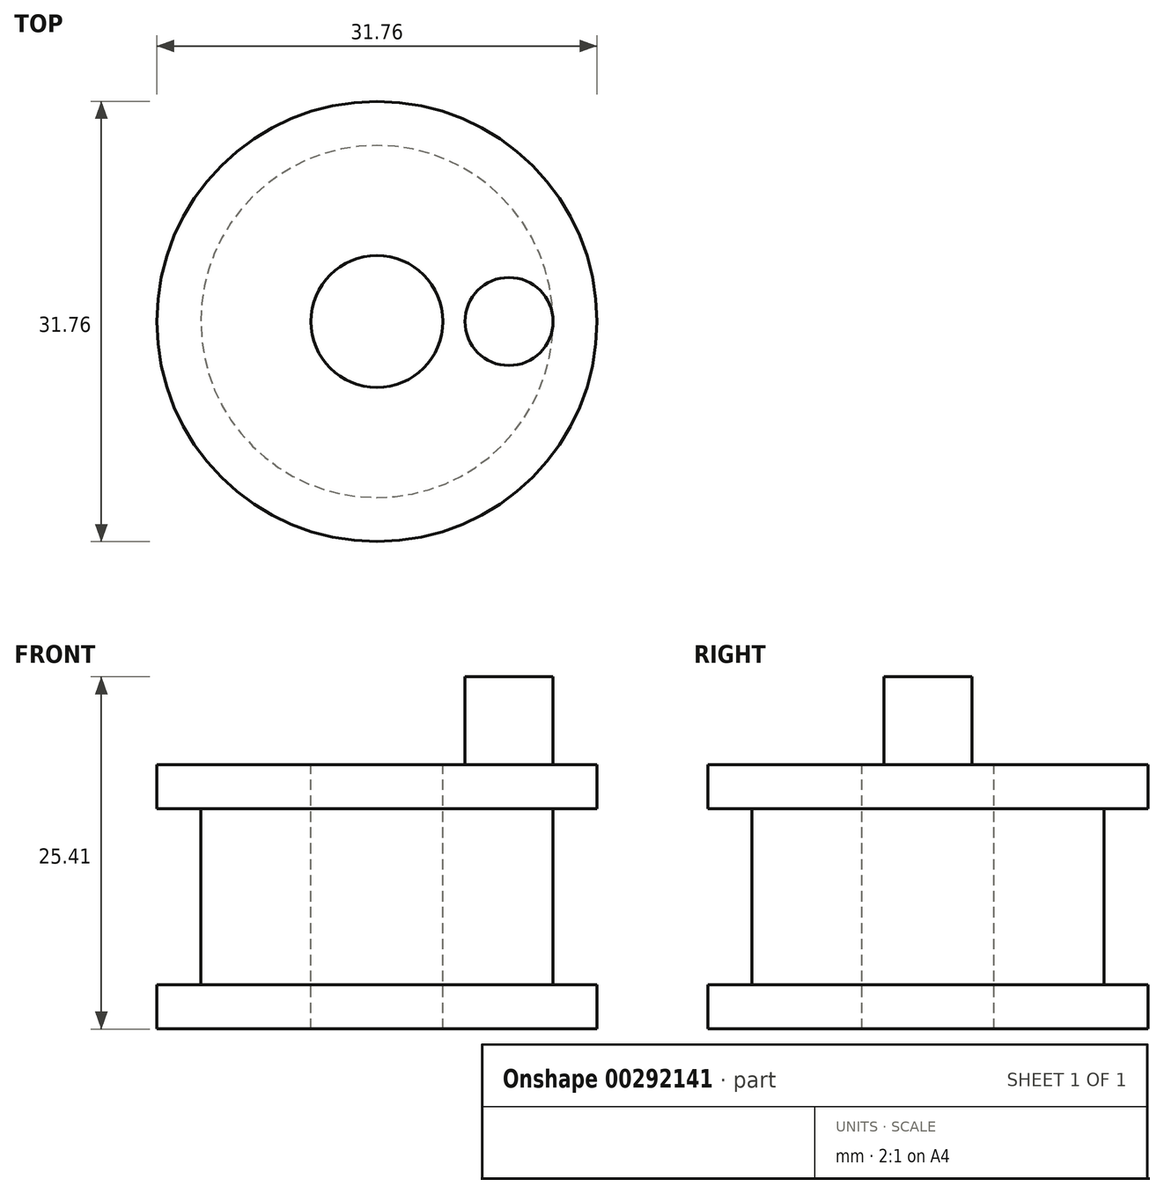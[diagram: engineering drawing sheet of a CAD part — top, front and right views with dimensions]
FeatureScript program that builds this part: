
annotation { "Feature Type Name" : "Feature", "Feature Type Description" : "" }
export const myFeature = defineFeature(function(context is Context, id is Id, definition is map)
    precondition{}
    {
        {
            var Q0;
            Q0=qCreatedBy(makeId("Front.planeOp"),FACE);
            var sketch = newSketch(context, id + "F0", { "sketchPlane" : qUnion([Q0])});
            skLineSegment(sketch, "E0", {"start": v(4.76, 0) * mm, "end": v(12.7, 0) * mm});
            skLineSegment(sketch, "E1", {"start": v(12.7, 0) * mm, "end": v(12.7, 6.35) * mm});
            skLineSegment(sketch, "E2", {"start": v(12.7, 6.35) * mm, "end": v(15.88, 6.35) * mm});
            skLineSegment(sketch, "E3", {"start": v(4.76, 0) * mm, "end": v(4.76, 9.52) * mm});
            skLineSegment(sketch, "E4", {"start": v(15.88, 6.35) * mm, "end": v(15.88, 9.53) * mm});
            skLineSegment(sketch, "E5", {"start": v(4.76, 9.53) * mm, "end": v(15.88, 9.53) * mm});
            skLineSegment(sketch, "E6", {"start": v(4.76, 0) * mm, "end": v(4.76, -9.53) * mm});
            skLineSegment(sketch, "E7", {"start": v(4.76, -9.53) * mm, "end": v(15.88, -9.53) * mm});
            skLineSegment(sketch, "E8", {"start": v(15.88, -9.52) * mm, "end": v(15.88, -6.35) * mm});
            skLineSegment(sketch, "E9", {"start": v(15.88, -6.35) * mm, "end": v(12.7, -6.35) * mm});
            skLineSegment(sketch, "E10", {"start": v(12.7, 0) * mm, "end": v(12.7, -6.35) * mm});
            skLineSegment(sketch, "E11", {"start": v(0, 11.73) * mm, "end": v(0, -15.5) * mm});
            skSolve(sketch);
        }
        {
            var Q0;
            Q0 = qSketchRegion(id + "F0", true);
            var Q1;
            Q1=sQuery(id+"F0.wireOp",EDGE,"E11");
            revolve(context, id + "F1", {"entities" : qUnion([Q0]), "axis" : qUnion([Q1]), "revolveType" : RevolveType.FULL});
        }
        {
            var Q0;
            Q0=qCreatedBy(makeId("Top.planeOp"),FACE);
            var sketch = newSketch(context, id + "F2", { "sketchPlane" : qUnion([Q0])});
            skCircle(sketch, "E12", {"center": v(9.53, 0) * mm, "radius": 3.18 * mm});
            skSolve(sketch);
        }
        {
            var Q0;
            Q0 = qSketchRegion(id + "F2", true);
            extrude(context, id + "F3", {"entities" : qUnion([Q0]), "operationType" : NewBodyOperationType.ADD, "depth" : 15.88 * mm});
        }
    });
